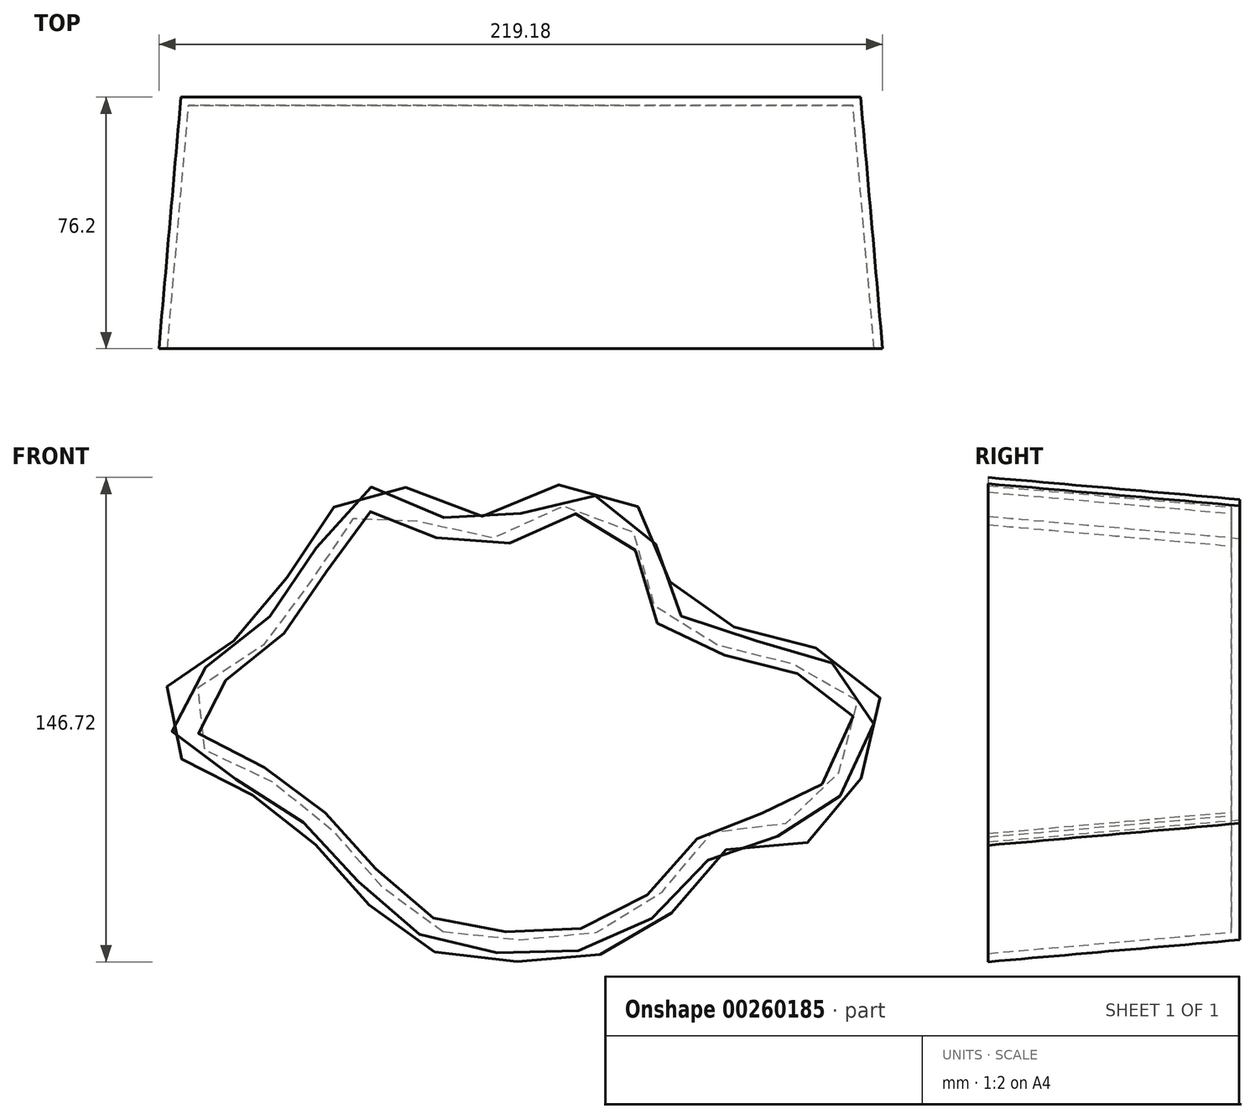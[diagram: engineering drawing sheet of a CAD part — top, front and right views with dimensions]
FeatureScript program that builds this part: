
annotation { "Feature Type Name" : "Feature", "Feature Type Description" : "" }
export const myFeature = defineFeature(function(context is Context, id is Id, definition is map)
    precondition{}
    {
        {
            var Q0;
            Q0=qCreatedBy(makeId("Front.planeOp"),FACE);
            var sketch = newSketch(context, id + "F0", { "sketchPlane" : qUnion([Q0])});
            skPoint(sketch, "E0.visualSharp", {"position": v(-74.98, 49.23) * mm});
            skPoint(sketch, "E1.visualSharp", {"position": v(77.42, 49.23) * mm});
            skPoint(sketch, "E2.visualSharp", {"position": v(77.42, -52.37) * mm});
            skPoint(sketch, "E3.visualSharp", {"position": v(-74.98, -52.37) * mm});
            skFitSpline(sketch, "E4", {"points": [v(0, 53.7) * mm, v(-23.28, 55.36) * mm, v(-35.1, 61.88) * mm, v(-41.78, 63.92) * mm, v(-58.24, 43.25) * mm, v(-66.69, 30.8) * mm, v(-77.59, 17.91) * mm, v(-95.4, 6.84) * mm, v(-100.06, 0) * mm, v(-94.7, -10.09) * mm, v(-85.12, -15.5) * mm, v(-78.43, -17.79) * mm, v(-73.08, -20.72) * mm, v(-54.57, -35.59) * mm, v(-42.74, -49.3) * mm, v(-20.66, -66.64) * mm, v(-1.94, -68.99) * mm, v(28.8, -65.82) * mm, v(55.5, -43.63) * mm, v(66.19, -33.2) * mm, v(85.8, -33.76) * mm, v(92.91, -27.77) * mm, v(104.68, 3.68) * mm, v(52.02, 23.83) * mm, v(41.13, 40.05) * mm, v(37.32, 53.93) * mm, v(15.26, 62.11) * mm, v(0, 53.7) * mm]});
            skSolve(sketch);
        }
        {
            var Q0;
            Q0 = qSketchRegion(id + "F0", true);
            extrude(context, id + "F1", {"entities" : qUnion([Q0]), "depth" : 76.2 * mm, "hasDraft" : true, "draftAngle" : 5 * degree});
        }
        {
            var Q0;
            Q0=makeQuery(id+"F1.opExtrude","CAP_FACE",FACE,{"disambiguationData":[OSD([sQuery(id+"F0.wireOp",EDGE,"E4")])],"isStart":false});
            shell(context, id + "F2", {"entities" : qUnion([Q0]), "thickness" : 2.54 * mm});
        }
    });
